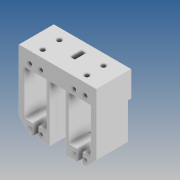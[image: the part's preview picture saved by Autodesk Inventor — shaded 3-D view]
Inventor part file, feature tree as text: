
AUTODESK INVENTOR PART (.ipt)
format: ipt  version: 2020 (Build 240168000, 168)  size: 486,912 bytes
history: native  units: mm
features: sketch x7, extrude x6, projected_geometry x4, hole x2, chamfer x2, other x1
ambient origin geometry x8: Origin, YZ Plane, XZ Plane, XY Plane, X Axis, Y Axis, Z Axis, Center Point
bodies: Body1 (feature_tree)
feature tree (22):
  other  "솔리드1"
  sketch  "스케치1"
  extrude  "돌출1"  Depth=20.0mm
  hole  "구멍1"  [1 undecoded]
  extrude  "돌출2"  Depth=20.0mm
  extrude  "돌출3"  Depth=5.0mm
  extrude  "돌출4"  Depth=5.0mm
  hole  "구멍2"  [1 undecoded]
  extrude  "돌출5"  Depth=5.0mm
  extrude  "돌출6"  Depth=5.0mm
  chamfer  "모따기1"  Distance=5.0mm
  chamfer  "모따기2"  Distance=5.0mm
  sketch  "스케치3"
  projected_geometry  "투영된 루프1"
  sketch  "스케치4"
  sketch  "스케치6"
  sketch  "스케치7"
  sketch  "스케치8"
  projected_geometry  "투영된 루프2"
  projected_geometry  "투영된 루프3"
  projected_geometry  "투영된 루프4"
  sketch  "스케치9"
note: 2 required parameter values undecoded (feature->parameter linkage not recoverable at this tier; creation-order binding heuristic only, values carry confidence <= 0.55)
